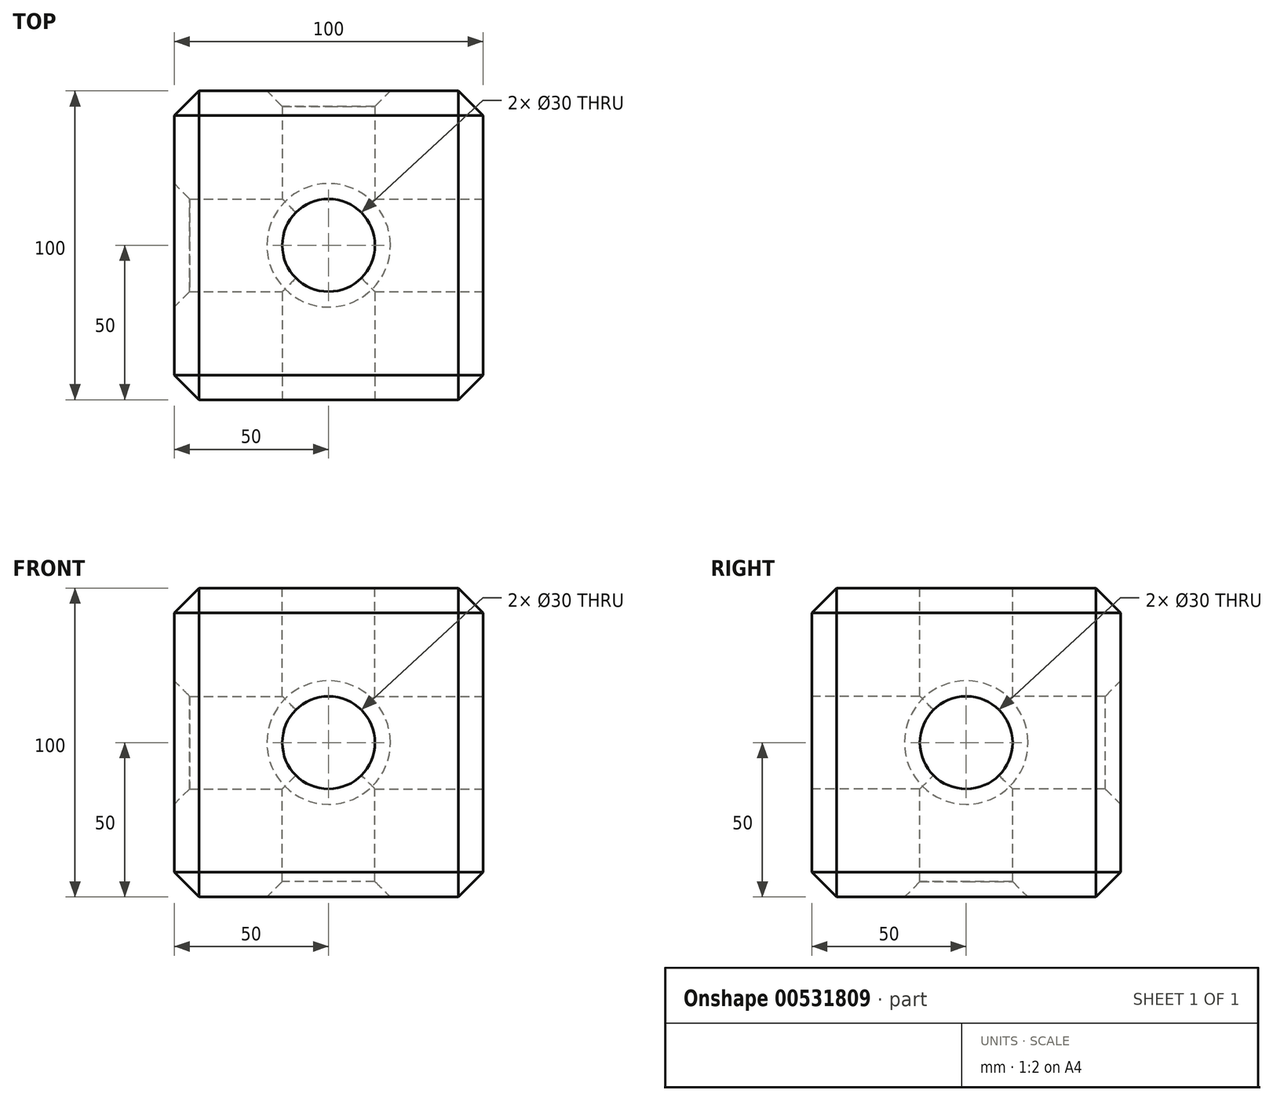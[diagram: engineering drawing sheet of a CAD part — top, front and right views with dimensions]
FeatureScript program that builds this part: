
annotation { "Feature Type Name" : "Feature", "Feature Type Description" : "" }
export const myFeature = defineFeature(function(context is Context, id is Id, definition is map)
    precondition{}
    {
        {
            var Q0;
            Q0=qCreatedBy(makeId("Front.planeOp"),FACE);
            var sketch = newSketch(context, id + "F0", { "sketchPlane" : qUnion([Q0])});
            skLineSegment(sketch, "E0.bottom", {"start": v(0, 0) * mm, "end": v(-100, 0) * mm});
            skLineSegment(sketch, "E0.top", {"start": v(0, -100) * mm, "end": v(-100, -100) * mm});
            skLineSegment(sketch, "E0.left", {"start": v(0, 0) * mm, "end": v(0, -100) * mm});
            skLineSegment(sketch, "E0.right", {"start": v(-100, 0) * mm, "end": v(-100, -100) * mm});
            skCircle(sketch, "E1", {"center": v(-50, -50) * mm, "radius": 15 * mm});
            skSolve(sketch);
        }
        {
            var Q0;
            Q0=makeQuery(id+"F0.imprint","IMPRINT",FACE,{"disambiguationData":[TD([[makeQuery(id+"F0.imprint","IMPRINT",EDGE,{"derivedFrom":sQuery(id+"F0.wireOp",EDGE,"E1")}),1.0]])]});
            var Q1;
            Q1=makeQuery(id+"F0.imprint","IMPRINT",FACE,{"disambiguationData":[TD([[makeQuery(id+"F0.imprint","IMPRINT",EDGE,{"derivedFrom":sQuery(id+"F0.wireOp",EDGE,"E0.bottom")}),1.0]])]});
            extrude(context, id + "F1", {"entities" : qUnion([Q0, Q1]), "oppositeDirection" : true, "depth" : 100 * mm, "offsetDistance" : 25 * mm});
        }
        {
            var Q0;
            Q0=makeQuery(id+"F1.opExtrude","SWEPT_FACE",FACE,{"disambiguationData":[OSD([sQuery(id+"F0.wireOp",EDGE,"E0.left")])]});
            var sketch = newSketch(context, id + "F2", { "sketchPlane" : qUnion([Q0])});
            skLineSegment(sketch, "E2", {"start": v(50, 0) * mm, "end": v(50, -100) * mm, "construction": true});
            skCircle(sketch, "E3", {"center": v(50, -50) * mm, "radius": 17.54 * mm, "construction": true});
            skCircle(sketch, "E4", {"center": v(50, -50) * mm, "radius": 15 * mm});
            skSolve(sketch);
        }
        {
            var Q0;
            Q0=makeQuery(id+"F2.imprint","IMPRINT",FACE,{"disambiguationData":[TD([[makeQuery(id+"F2.imprint","IMPRINT",EDGE,{"derivedFrom":sQuery(id+"F2.wireOp",EDGE,"E4")}),1.0]])]});
            extrude(context, id + "F3", {"entities" : qUnion([Q0]), "operationType" : NewBodyOperationType.REMOVE, "oppositeDirection" : true, "depth" : 300 * mm, "offsetDistance" : 25 * mm});
        }
        {
            var Q0;
            Q0=makeQuery(id+"F1.opExtrude","CAP_FACE",FACE,{"disambiguationData":[OSD([sQuery(id+"F0.wireOp",EDGE,"E0.bottom"),sQuery(id+"F0.wireOp",EDGE,"E0.top"),sQuery(id+"F0.wireOp",EDGE,"E0.left"),sQuery(id+"F0.wireOp",EDGE,"E0.right")])],"isStart":true});
            var sketch = newSketch(context, id + "F4", { "sketchPlane" : qUnion([Q0])});
            skLineSegment(sketch, "E5", {"start": v(-50, 0) * mm, "end": v(-50, -100) * mm, "construction": true});
            skCircle(sketch, "E6", {"center": v(-50, -50) * mm, "radius": 15 * mm});
            skSolve(sketch);
        }
        {
            var Q0;
            Q0=makeQuery(id+"F4.imprint","IMPRINT",FACE,{"disambiguationData":[TD([[makeQuery(id+"F4.imprint","IMPRINT",EDGE,{"derivedFrom":sQuery(id+"F4.wireOp",EDGE,"E6")}),1.0]])]});
            extrude(context, id + "F5", {"entities" : qUnion([Q0]), "operationType" : NewBodyOperationType.REMOVE, "oppositeDirection" : true, "depth" : 300 * mm, "offsetDistance" : 25 * mm});
        }
        {
            var Q0;
            Q0=makeQuery(id+"F1.opExtrude","SWEPT_FACE",FACE,{"disambiguationData":[OSD([sQuery(id+"F0.wireOp",EDGE,"E0.bottom")])]});
            var sketch = newSketch(context, id + "F6", { "sketchPlane" : qUnion([Q0])});
            skLineSegment(sketch, "E7", {"start": v(-50, 100) * mm, "end": v(-50, 0) * mm, "construction": true});
            skCircle(sketch, "E8", {"center": v(-50, 50) * mm, "radius": 15 * mm});
            skSolve(sketch);
        }
        {
            var Q0;
            Q0 = qSketchRegion(id + "F6", true);
            extrude(context, id + "F7", {"entities" : qUnion([Q0]), "operationType" : NewBodyOperationType.REMOVE, "oppositeDirection" : true, "depth" : 300 * mm, "offsetDistance" : 25 * mm});
        }
        {
            var Q0;
            Q0=makeQuery(id+"F1.opExtrude","CAP_EDGE",EDGE,{"disambiguationData":[OSD([sQuery(id+"F0.wireOp",EDGE,"E0.bottom")])],"isStart":true});
            var Q1;
            Q1=makeQuery(id+"F1.opExtrude","CAP_EDGE",EDGE,{"disambiguationData":[OSD([sQuery(id+"F0.wireOp",EDGE,"E0.left")])],"isStart":true});
            var Q2;
            Q2=makeQuery(id+"F1.opExtrude","CAP_EDGE",EDGE,{"disambiguationData":[OSD([sQuery(id+"F0.wireOp",EDGE,"E0.right")])],"isStart":true});
            var Q3;
            Q3=makeQuery(id+"F1.opExtrude","CAP_EDGE",EDGE,{"disambiguationData":[OSD([sQuery(id+"F0.wireOp",EDGE,"E0.top")])],"isStart":true});
            var Q4;
            Q4=makeQuery(id+"F1.opExtrude","SWEPT_EDGE",EDGE,{"disambiguationData":[OSD([sQuery(id+"F0.wireOp",EDGE,"E0.bottom"),sQuery(id+"F0.wireOp",EDGE,"E0.right")])]});
            var Q5;
            Q5=makeQuery(id+"F1.opExtrude","CAP_EDGE",EDGE,{"disambiguationData":[OSD([sQuery(id+"F0.wireOp",EDGE,"E0.right")])],"isStart":false});
            var Q6;
            Q6=makeQuery(id+"F1.opExtrude","SWEPT_EDGE",EDGE,{"disambiguationData":[OSD([sQuery(id+"F0.wireOp",EDGE,"E0.top"),sQuery(id+"F0.wireOp",EDGE,"E0.right")])]});
            var Q7;
            Q7=makeQuery(id+"F1.opExtrude","SWEPT_EDGE",EDGE,{"disambiguationData":[OSD([sQuery(id+"F0.wireOp",EDGE,"E0.bottom"),sQuery(id+"F0.wireOp",EDGE,"E0.left")])]});
            var Q8;
            Q8=makeQuery(id+"F1.opExtrude","CAP_EDGE",EDGE,{"disambiguationData":[OSD([sQuery(id+"F0.wireOp",EDGE,"E0.left")])],"isStart":false});
            var Q9;
            Q9=makeQuery(id+"F1.opExtrude","SWEPT_EDGE",EDGE,{"disambiguationData":[OSD([sQuery(id+"F0.wireOp",EDGE,"E0.top"),sQuery(id+"F0.wireOp",EDGE,"E0.left")])]});
            var Q10;
            Q10=makeQuery(id+"F1.opExtrude","CAP_EDGE",EDGE,{"disambiguationData":[OSD([sQuery(id+"F0.wireOp",EDGE,"E0.top")])],"isStart":false});
            var Q11;
            Q11=makeQuery(id+"F1.opExtrude","CAP_EDGE",EDGE,{"disambiguationData":[OSD([sQuery(id+"F0.wireOp",EDGE,"E0.bottom")])],"isStart":false});
            chamfer(context, id + "F8", {"entities" : qUnion([Q0, Q1, Q2, Q3, Q4, Q5, Q6, Q7, Q8, Q9, Q10, Q11]), "width" : 8 * mm, "tangentPropagation" : true});
        }
        {
            var Q0;
            Q0=makeQuery(id+"F5.boolean.opBoolean","COPY",EDGE,{"derivedFrom":makeQuery(id+"F5.opExtrude","CAP_EDGE",EDGE,{"disambiguationData":[OSD([sQuery(id+"F4.wireOp",EDGE,"E6")])],"isStart":true})});
            var Q1;
            Q1=makeQuery(id+"F3.boolean.opBoolean","COPY",EDGE,{"derivedFrom":makeQuery(id+"F3.opExtrude","CAP_EDGE",EDGE,{"disambiguationData":[OSD([sQuery(id+"F2.wireOp",EDGE,"E4")])],"isStart":true})});
            var Q2;
            Q2=makeQuery(id+"F7.boolean.opBoolean","COPY",EDGE,{"derivedFrom":makeQuery(id+"F7.opExtrude","CAP_EDGE",EDGE,{"disambiguationData":[OSD([sQuery(id+"F6.wireOp",EDGE,"E8")])],"isStart":true})});
            var Q3;
            Q3=makeQuery(id+"F3.boolean.opBoolean","INTERSECT",EDGE,{"derivedFrom":[makeQuery(id+"F1.opExtrude","SWEPT_FACE",FACE,{"disambiguationData":[OSD([sQuery(id+"F0.wireOp",EDGE,"E0.right")])]}),makeQuery(id+"F3.opExtrude","SWEPT_FACE",FACE,{"disambiguationData":[OSD([sQuery(id+"F2.wireOp",EDGE,"E4")])]})]});
            var Q4;
            Q4=makeQuery(id+"F7.boolean.opBoolean","INTERSECT",EDGE,{"derivedFrom":[makeQuery(id+"F1.opExtrude","SWEPT_FACE",FACE,{"disambiguationData":[OSD([sQuery(id+"F0.wireOp",EDGE,"E0.top")])]}),makeQuery(id+"F7.opExtrude","SWEPT_FACE",FACE,{"disambiguationData":[OSD([sQuery(id+"F6.wireOp",EDGE,"E8")])]})]});
            var Q5;
            Q5=makeQuery(id+"F5.boolean.opBoolean","INTERSECT",EDGE,{"derivedFrom":[makeQuery(id+"F1.opExtrude","CAP_FACE",FACE,{"disambiguationData":[OSD([sQuery(id+"F0.wireOp",EDGE,"E0.bottom"),sQuery(id+"F0.wireOp",EDGE,"E0.top"),sQuery(id+"F0.wireOp",EDGE,"E0.left"),sQuery(id+"F0.wireOp",EDGE,"E0.right")])],"isStart":false}),makeQuery(id+"F5.opExtrude","SWEPT_FACE",FACE,{"disambiguationData":[OSD([sQuery(id+"F4.wireOp",EDGE,"E6")])]})]});
            chamfer(context, id + "F9", {"entities" : qUnion([Q0, Q1, Q2, Q3, Q4, Q5]), "width" : 5 * mm, "tangentPropagation" : true});
        }
    });
